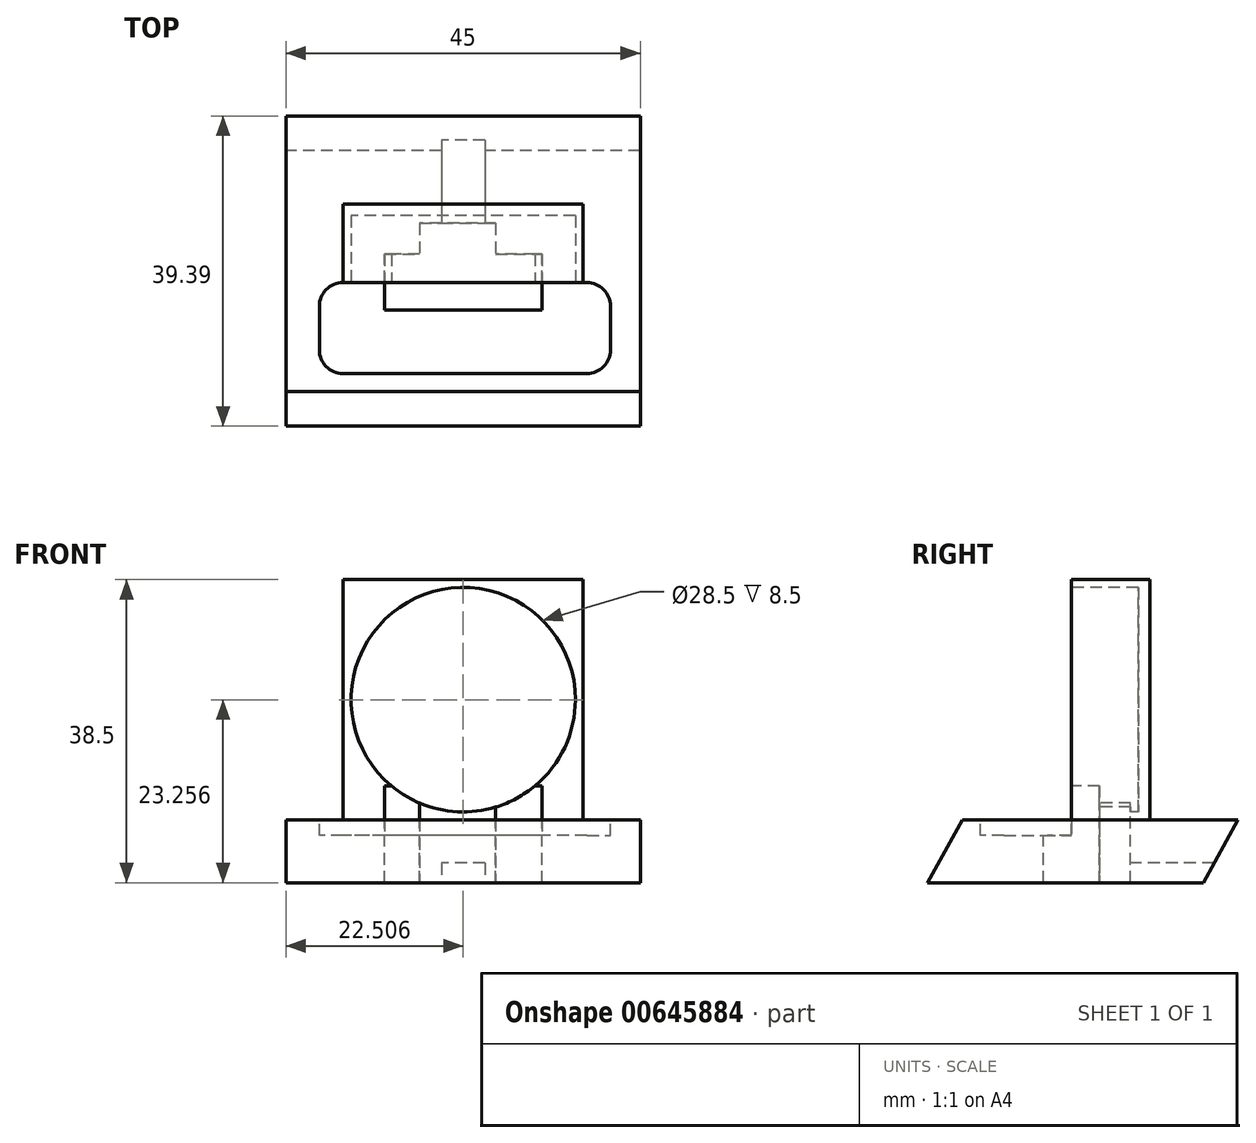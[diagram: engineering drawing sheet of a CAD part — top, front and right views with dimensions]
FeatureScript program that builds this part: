
annotation { "Feature Type Name" : "Feature", "Feature Type Description" : "" }
export const myFeature = defineFeature(function(context is Context, id is Id, definition is map)
    precondition{}
    {
        {
            var Q0;
            Q0=qCreatedBy(makeId("Right.planeOp"),FACE);
            var sketch = newSketch(context, id + "F0", { "sketchPlane" : qUnion([Q0])});
            skLineSegment(sketch, "E0", {"start": v(-37.2, 4) * mm, "end": v(-35, 8) * mm});
            skLineSegment(sketch, "E1", {"start": v(-35, 8) * mm, "end": v(0, 8) * mm});
            skLineSegment(sketch, "E2", {"start": v(0, 8) * mm, "end": v(-2.2, 4) * mm});
            skLineSegment(sketch, "E3", {"start": v(-37.2, 4) * mm, "end": v(-39.39, 0) * mm});
            skLineSegment(sketch, "E4", {"start": v(-2.2, 4) * mm, "end": v(-4.39, 0) * mm});
            skLineSegment(sketch, "E5", {"start": v(-4.39, 0) * mm, "end": v(-39.39, 0) * mm});
            skSolve(sketch);
        }
        {
            var Q0;
            Q0 = qSketchRegion(id + "F0", true);
            extrude(context, id + "F1", {"entities" : qUnion([Q0]), "depth" : 45 * mm, "offsetDistance" : 25.4 * mm});
        }
        {
            var Q0;
            Q0=makeQuery(id+"F1.opExtrude","SWEPT_FACE",FACE,{"disambiguationData":[OSD([sQuery(id+"F0.wireOp",EDGE,"E1")])]});
            var sketch = newSketch(context, id + "F2", { "sketchPlane" : qUnion([Q0])});
            skLineSegment(sketch, "E6.bottom", {"start": v(41.23, -32.7) * mm, "end": v(4.23, -32.7) * mm});
            skLineSegment(sketch, "E6.top", {"start": v(41.23, -21.15) * mm, "end": v(4.23, -21.15) * mm});
            skLineSegment(sketch, "E6.left", {"start": v(41.23, -32.7) * mm, "end": v(41.23, -21.15) * mm});
            skLineSegment(sketch, "E6.right", {"start": v(4.23, -32.7) * mm, "end": v(4.23, -21.15) * mm});
            skPoint(sketch, "E6.middle", {"position": v(22.73, -26.92) * mm});
            skSolve(sketch);
        }
        {
            var Q0;
            {var subQ5=sQuery(id+"F2.wireOp",EDGE,"E6.right");Q0=makeQuery(id+"F2.imprint","IMPRINT",FACE,{"disambiguationData":[TD([[makeQuery(id+"F2.imprint","IMPRINT",EDGE,{"derivedFrom":subQ5}),-1.0]])]});}
            var Q1;
            {var subQ5=sQuery(id+"F2.wireOp",EDGE,"E6.left");Q1=makeQuery(id+"F2.imprint","IMPRINT",FACE,{"disambiguationData":[TD([[makeQuery(id+"F2.imprint","IMPRINT",EDGE,{"derivedFrom":subQ5}),1.0]])]});}
            extrude(context, id + "F3", {"entities" : qUnion([Q0, Q1]), "operationType" : NewBodyOperationType.REMOVE, "oppositeDirection" : true, "depth" : 2 * mm, "offsetDistance" : 25.4 * mm});
        }
        {
            var Q0;
            Q0=makeQuery(id+"F3.boolean.opBoolean","COPY",EDGE,{"derivedFrom":makeQuery(id+"F3.opExtrude","SWEPT_EDGE",EDGE,{"disambiguationData":[OSD([sQuery(id+"F2.wireOp",EDGE,"E6.top"),sQuery(id+"F2.wireOp",EDGE,"E6.right")])]})});
            var Q1;
            Q1=makeQuery(id+"F3.boolean.opBoolean","COPY",EDGE,{"derivedFrom":makeQuery(id+"F3.opExtrude","SWEPT_EDGE",EDGE,{"disambiguationData":[OSD([sQuery(id+"F2.wireOp",EDGE,"E6.bottom"),sQuery(id+"F2.wireOp",EDGE,"E6.right")])]})});
            var Q2;
            Q2=makeQuery(id+"F3.boolean.opBoolean","COPY",EDGE,{"derivedFrom":makeQuery(id+"F3.opExtrude","SWEPT_EDGE",EDGE,{"disambiguationData":[OSD([sQuery(id+"F2.wireOp",EDGE,"E6.top"),sQuery(id+"F2.wireOp",EDGE,"E6.left")])]})});
            var Q3;
            Q3=makeQuery(id+"F3.boolean.opBoolean","COPY",EDGE,{"derivedFrom":makeQuery(id+"F3.opExtrude","SWEPT_EDGE",EDGE,{"disambiguationData":[OSD([sQuery(id+"F2.wireOp",EDGE,"E6.bottom"),sQuery(id+"F2.wireOp",EDGE,"E6.left")])]})});
            fillet(context, id + "F4", {"entities" : qUnion([Q0, Q1, Q2, Q3]), "radius" : 3 * mm, "tangentPropagation" : true, "allowEdgeOverflow" : false});
        }
        {
            var Q0;
            Q0=makeQuery(id+"F1.opExtrude","SWEPT_FACE",FACE,{"disambiguationData":[OSD([sQuery(id+"F0.wireOp",EDGE,"E1")])]});
            var sketch = newSketch(context, id + "F5", { "sketchPlane" : qUnion([Q0])});
            skLineSegment(sketch, "E7.bottom", {"start": v(37.75, -21.15) * mm, "end": v(7.25, -21.15) * mm});
            skLineSegment(sketch, "E7.top", {"start": v(37.75, -11.15) * mm, "end": v(7.25, -11.15) * mm});
            skLineSegment(sketch, "E7.left", {"start": v(37.75, -21.15) * mm, "end": v(37.75, -11.15) * mm});
            skLineSegment(sketch, "E7.right", {"start": v(7.25, -21.15) * mm, "end": v(7.25, -11.15) * mm});
            skPoint(sketch, "E7.middle", {"position": v(22.5, -16.15) * mm});
            skSolve(sketch);
        }
        {
            var Q0;
            Q0 = qSketchRegion(id + "F5", true);
            extrude(context, id + "F6", {"entities" : qUnion([Q0]), "operationType" : NewBodyOperationType.ADD, "depth" : 30.5 * mm, "offsetDistance" : 25.4 * mm});
        }
        {
            var Q0;
            Q0=makeQuery(id+"F6.boolean.opBoolean","MERGE",FACE,{"derivedFrom":[makeQuery(id+"F3.boolean.opBoolean","COPY",FACE,{"derivedFrom":makeQuery(id+"F3.opExtrude","SWEPT_FACE",FACE,{"disambiguationData":[OSD([sQuery(id+"F2.wireOp",EDGE,"E6.top")])]})}),makeQuery(id+"F6.opExtrude","SWEPT_FACE",FACE,{"disambiguationData":[OSD([sQuery(id+"F5.wireOp",EDGE,"E7.bottom")])]})]});
            var sketch = newSketch(context, id + "F7", { "sketchPlane" : qUnion([Q0])});
            skCircle(sketch, "E8", {"center": v(22.5, 23.26) * mm, "radius": 14.25 * mm});
            skSolve(sketch);
        }
        {
            var Q0;
            Q0 = qSketchRegion(id + "F7", true);
            extrude(context, id + "F8", {"entities" : qUnion([Q0]), "operationType" : NewBodyOperationType.REMOVE, "oppositeDirection" : true, "depth" : 8.5 * mm, "offsetDistance" : 25.4 * mm});
        }
        {
            var Q0;
            Q0=qCreatedBy(makeId("Top.planeOp"),FACE);
            cPlane(context, id + "F9", {"entities" : qUnion([Q0]), "cplaneType" : CPlaneType.OFFSET, "offset" : 12.32 * mm, "width" : 152.4 * mm, "height" : 152.4 * mm});
        }
        {
            var Q0;
            Q0=qCreatedBy(id+"F9.planeOp",FACE);
            var sketch = newSketch(context, id + "F10", { "sketchPlane" : qUnion([Q0])});
            skLineSegment(sketch, "E9.bottom", {"start": v(32.5, -24.66) * mm, "end": v(12.5, -24.66) * mm});
            skLineSegment(sketch, "E9.top", {"start": v(32.5, -17.55) * mm, "end": v(12.5, -17.55) * mm});
            skLineSegment(sketch, "E9.left", {"start": v(32.5, -24.66) * mm, "end": v(32.5, -17.55) * mm});
            skLineSegment(sketch, "E9.right", {"start": v(12.5, -24.66) * mm, "end": v(12.5, -17.55) * mm});
            skPoint(sketch, "E9.middle", {"position": v(22.5, -21.1) * mm});
            skSolve(sketch);
        }
        {
            var Q0;
            Q0 = qSketchRegion(id + "F10", true);
            extrude(context, id + "F11", {"entities" : qUnion([Q0]), "operationType" : NewBodyOperationType.REMOVE, "oppositeDirection" : true, "depth" : 25.4 * mm, "offsetDistance" : 25.4 * mm});
        }
        {
            var Q0;
            Q0=makeQuery(id+"F1.opExtrude","SWEPT_FACE",FACE,{"disambiguationData":[OSD([sQuery(id+"F0.wireOp",EDGE,"E5")])]});
            var sketch = newSketch(context, id + "F12", { "sketchPlane" : qUnion([Q0])});
            skLineSegment(sketch, "E10.bottom", {"start": v(25.27, -8.04) * mm, "end": v(19.74, -8.04) * mm});
            skLineSegment(sketch, "E10.left", {"start": v(25.27, -8.04) * mm, "end": v(25.27, 17.58) * mm});
            skLineSegment(sketch, "E10.right", {"start": v(19.74, -8.04) * mm, "end": v(19.74, 17.58) * mm});
            skPoint(sketch, "E10.middle", {"position": v(22.5, 17.58) * mm});
            skLineSegment(sketch, "E11", {"start": v(19.74, 17.58) * mm, "end": v(25.27, 17.58) * mm});
            skSolve(sketch);
        }
        {
            var Q0;
            Q0 = qSketchRegion(id + "F12", true);
            extrude(context, id + "F13", {"entities" : qUnion([Q0]), "operationType" : NewBodyOperationType.REMOVE, "oppositeDirection" : true, "depth" : 2.5 * mm, "offsetDistance" : 25.4 * mm});
        }
        {
            var Q0;
            Q0=qCreatedBy(id+"F9.planeOp",FACE);
            var sketch = newSketch(context, id + "F14", { "sketchPlane" : qUnion([Q0])});
            skLineSegment(sketch, "E12.bottom", {"start": v(26.64, -22.95) * mm, "end": v(16.96, -22.95) * mm});
            skLineSegment(sketch, "E12.top", {"start": v(26.64, -13.62) * mm, "end": v(16.96, -13.62) * mm});
            skLineSegment(sketch, "E12.left", {"start": v(26.64, -22.95) * mm, "end": v(26.64, -13.62) * mm});
            skLineSegment(sketch, "E12.right", {"start": v(16.96, -22.95) * mm, "end": v(16.96, -13.62) * mm});
            skPoint(sketch, "E12.middle", {"position": v(21.8, -18.28) * mm});
            skSolve(sketch);
        }
        {
            var Q0;
            Q0 = qSketchRegion(id + "F14", true);
            extrude(context, id + "F15", {"entities" : qUnion([Q0]), "operationType" : NewBodyOperationType.REMOVE, "oppositeDirection" : true, "depth" : 25.4 * mm, "offsetDistance" : 25.4 * mm});
        }
    });
